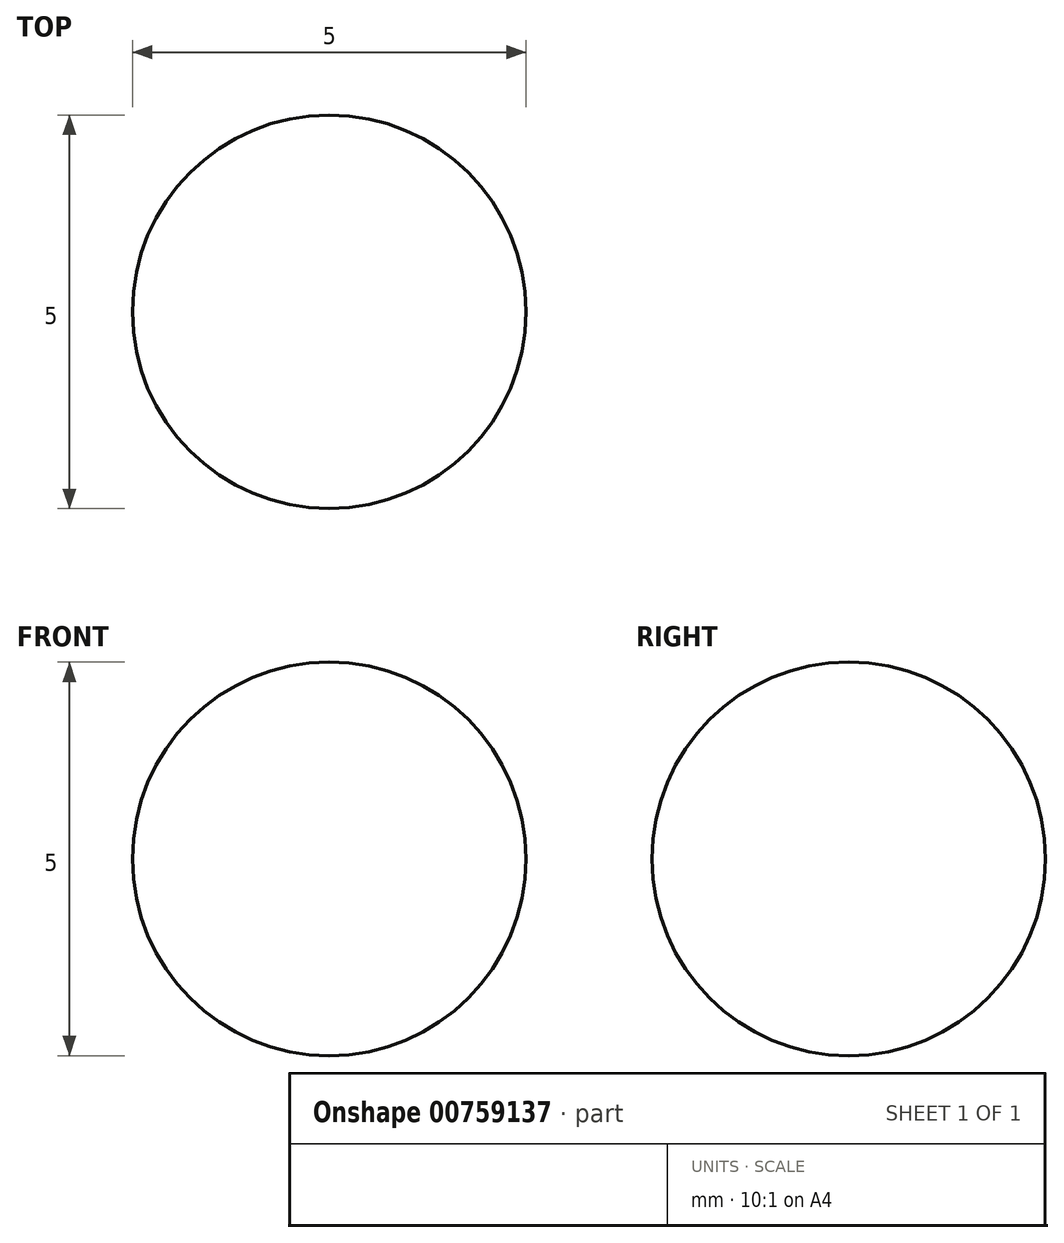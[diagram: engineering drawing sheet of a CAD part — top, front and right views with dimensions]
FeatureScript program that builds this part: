
annotation { "Feature Type Name" : "Feature", "Feature Type Description" : "" }
export const myFeature = defineFeature(function(context is Context, id is Id, definition is map)
    precondition{}
    {
        {
            var Q0;
            Q0=qCreatedBy(makeId("Top.planeOp"),FACE);
            var sketch = newSketch(context, id + "F0", { "sketchPlane" : qUnion([Q0])});
            skArc(sketch, "E0", {"start": v(0, 2.5) * mm, "mid": v(-2.5, 0) * mm, "end": v(0, -2.5) * mm});
            skLineSegment(sketch, "E1", {"start": v(0, 2.5) * mm, "end": v(0, -2.5) * mm});
            skSolve(sketch);
        }
        {
            var Q0;
            Q0=makeQuery(id+"F0.imprint","IMPRINT",FACE,{"disambiguationData":[TD([[makeQuery(id+"F0.imprint","IMPRINT",EDGE,{"derivedFrom":sQuery(id+"F0.wireOp",EDGE,"E0")}),1.0]])]});
            var Q1;
            Q1=sQuery(id+"F0.wireOp",EDGE,"E1");
            revolve(context, id + "F1", {"surfaceOperationType" : NewSurfaceOperationType.NEW, "entities" : qUnion([Q0]), "axis" : qUnion([Q1]), "revolveType" : RevolveType.FULL});
        }
    });
